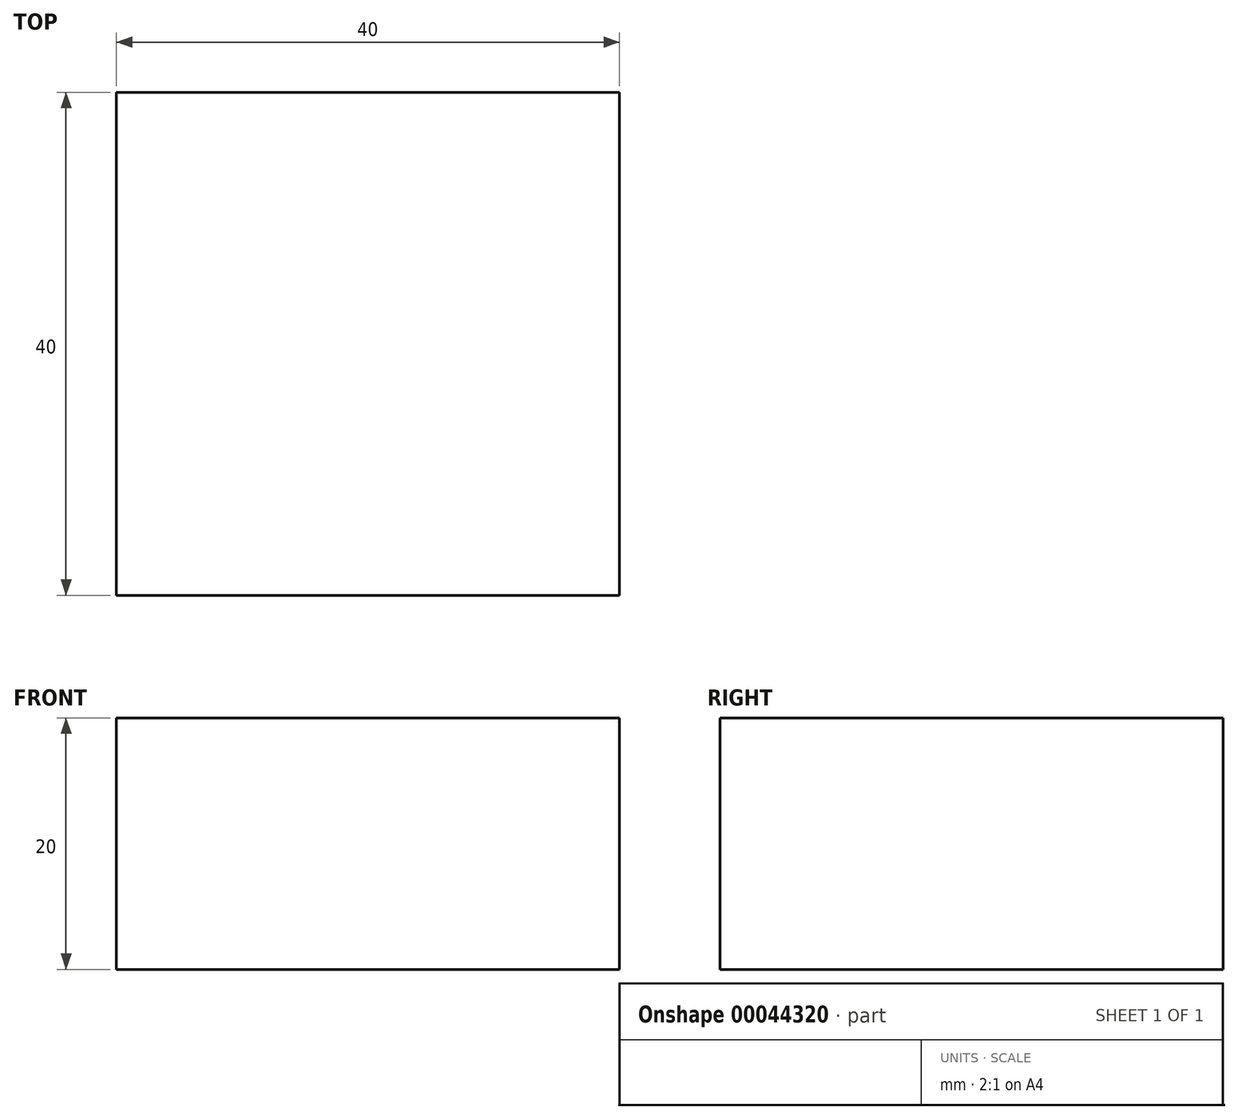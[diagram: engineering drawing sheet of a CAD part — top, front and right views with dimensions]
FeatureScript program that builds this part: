
annotation { "Feature Type Name" : "Feature", "Feature Type Description" : "" }
export const myFeature = defineFeature(function(context is Context, id is Id, definition is map)
    precondition{}
    {
        {
            var Q0;
            Q0=qCreatedBy(makeId("Top.planeOp"), FACE);
            var sketch = newSketch(context, id + "F0", { "sketchPlane" : qUnion([Q0])});
            skLineSegment(sketch, "E0.bottom", {"start": v(20, -20) * mm, "end": v(-20, -20) * mm});
            skLineSegment(sketch, "E0.top", {"start": v(20, 20) * mm, "end": v(-20, 20) * mm});
            skLineSegment(sketch, "E0.left", {"start": v(20, -20) * mm, "end": v(20, 20) * mm});
            skLineSegment(sketch, "E0.right", {"start": v(-20, -20) * mm, "end": v(-20, 20) * mm});
            skPoint(sketch, "E0.middle", {"position": v(0, 0) * mm});
            skSolve(sketch);
        }
        {
            var Q0;
            Q0 = qSketchRegion(id + "F0", true);
            extrude(context, id + "F1", {"entities" : qUnion([Q0]), "depth" : 20 * mm, "offsetDistance" : 25 * mm});
        }
    });
